# Revit family: BC_Hitachi_RPI-FSN3PE-16.0-20.0_LOD400
name_source: partatom
category: Equipement de génie climatique
revit_build: Autodesk Revit 2016 (Build: 20150220_1215(x64)
units: mm (PartAtom-declared; Revit-internal decimal feet)

## family parameters
Basée sur le plan de construction = Non
Cote de connecteur circulaire = Utiliser le diamètre
Couper avec des vides une fois chargée = Non
Numéro OmniClass = 23.75.00.00
Partagée = Non
Point de calcul de pièce = Non
Titre OmniClass = Climate Control (HVAC)
Toujours verticalement = Oui
Type d'élément = Normal

## types (2) — shared parameters
Air outlet distance = 25.00 mm
Description = Duct High pressure, Up to 220 Pa
Distance from left Drain pipe = 370.00 mm
Distance from left liquid pipe = 360.00 mm
Drain pipe Height = 20.00 mm
Fabricant = HITACHI
Fan motor type (output) = 1065 W
Frequency = 50 Hz
Gas pipe Height = 250.00 mm
Input Height = 324.00 mm
Input Width = 1376.00 mm
Liquid Diameter = 9.52 mm
Liquid pipe Height = 300.00 mm
Mass = 171.00 kg
Maximum AC Voltage = 253 V
Minimum AC Voltage = 207 V
Modèle = Ducted unit RPI-FSN3/4 - 16 to 20
Nominal Voltage = 230 V
Number of Poles = 1
Outlet Diameter = 25.00 mm
Output Height = 250.00 mm
Output Width = 1376.00 mm
Overall Depth = 423.00 mm
Overall Height = 1592.00 mm
Overall Width = 600.00 mm
Refrigerant = R410A

## per-type parameters (varying)
| type | Acoustic Pressure Level Maxi (dB) | Acoustic Pressure Level Mini (dB) | Air flow Speed (high/medium/low) m3/min) | Cooling Capacity | Distance from left Gas pipe | Gas Diameter | Heating Capacity | Maximum Air Flow | Minimum Air Flow | Product Code | Sound power max (dB(A)) | Usage Current |
| RPI - 16.0 FSN3PE | 56 | 53 | 132/120 | 45 kW | 370.00 mm | 19.05 mm | 50 kW | 132000.0 L/min | 120000.0 L/min | 7E425038 | 79 | 16 A |
| RPI - 20.0 FSN3PE | 57 | 54 | 150/137 | 63 kW | 360.00 mm | 22.20 mm | 63 kW | 150000.0 L/min | 137000.0 L/min | 7E425039 | 80 | 18 A |

note: column(s) folded — value = type name in every type: Commentaires du type

## geometry (parser evidence)
native form markers: Blend x2
no freeform markers — native parametric forms only
